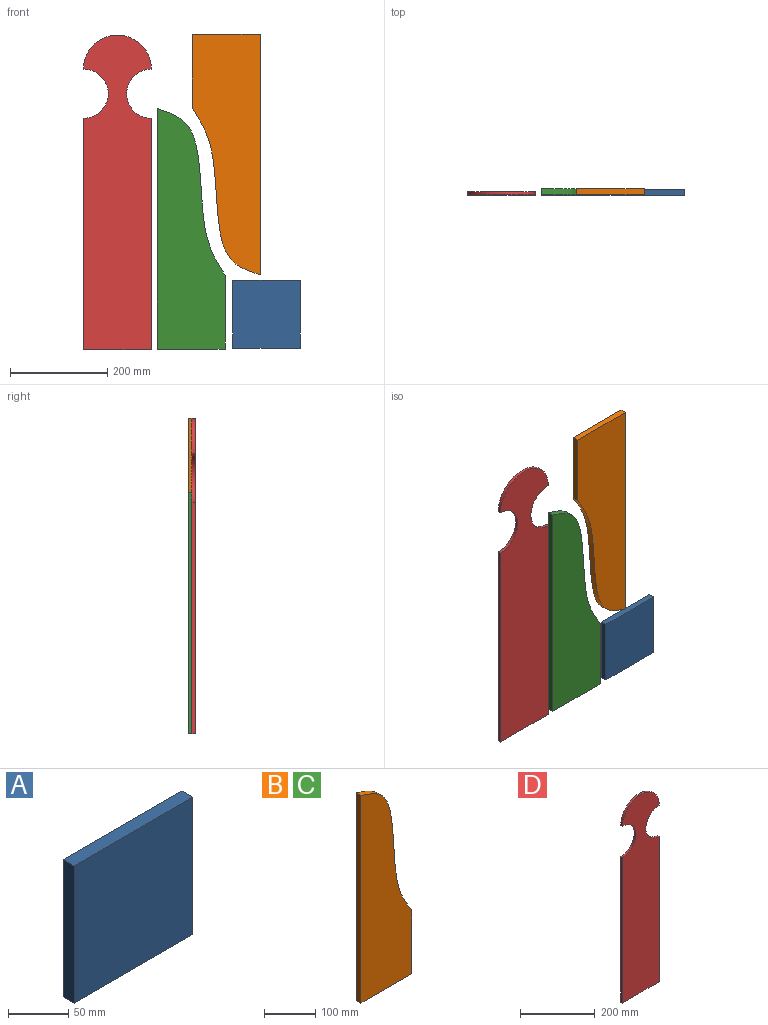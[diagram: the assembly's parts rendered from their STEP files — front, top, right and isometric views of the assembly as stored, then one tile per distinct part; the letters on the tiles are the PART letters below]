
ASSEMBLY  parts=4 mates=3
PART A: 6 faces, bbox 139.7x12.7x139.7 mm
  f0: plane 139.7x12.7mm, normal (-1,0,0), area 1774.2mm2, adj f1,f3,f4,f5
  f1: plane 139.7x12.7mm, normal (0,0,-1), area 1774.2mm2, adj f0,f2,f4,f5
  f2: plane 139.7x12.7mm, normal (1,0,0), area 1774.2mm2, adj f1,f3,f4,f5
  f3: plane 139.7x12.7mm, normal (0,0,1), area 1774.2mm2, adj f0,f2,f4,f5
  f4: plane 139.7x139.7mm, normal (0,-1,0), area 19516.1mm2, adj f0,f1,f2,f3
  f5: plane 139.7x139.7mm, normal (0,1,0), area 19516.1mm2, adj f0,f1,f2,f3
PART B: 6 faces, bbox 139.7x12.7x495.3 mm
  f0: extruded ~342.9x139.7mm, area 5021mm2, adj f1,f3,f4,f5
  f1: plane 495.3x12.7mm, normal (-1,0,0), area 6290.3mm2, adj f0,f2,f4,f5
  f2: plane 139.7x12.7mm, normal (0,0,-1), area 1774.2mm2, adj f1,f3,f4,f5
  f3: plane 152.4x12.7mm, normal (1,0,0), area 1935.5mm2, adj f0,f2,f4,f5
  f4: plane 495.3x139.7mm, normal (0,-1,0), area 52077.9mm2, adj f0,f1,f2,f3
  f5: plane 495.3x139.7mm, normal (0,1,0), area 52077.9mm2, adj f0,f1,f2,f3
PART C: same geometry as B
PART D: 8 faces, bbox 139.7x6.4x647.7 mm
  f0: cylinder r=69.85mm len=139.7mm, axis (0,1,0), area 1393.4mm2, adj f1,f5,f6,f7
  f1: cylinder r=50.8mm len=101.6mm, axis (0,1,0), area 1013.4mm2, adj f0,f2,f6,f7
  f2: plane 476.25x6.35mm, normal (-1,0,0), area 3024.2mm2, adj f1,f3,f6,f7
  f3: plane 139.7x6.35mm, normal (0,0,-1), area 887.1mm2, adj f2,f4,f6,f7
  f4: plane 476.25x6.35mm, normal (1,0,0), area 3024.2mm2, adj f3,f5,f6,f7
  f5: cylinder r=50.8mm len=101.6mm, axis (0,1,0), area 1013.4mm2, adj f0,f4,f6,f7
  f6: plane 647.7x139.7mm, normal (0,-1,0), area 80282.3mm2, adj f0,f1,f2,f3,f4,f5
  f7: plane 647.7x139.7mm, normal (0,1,0), area 80282.3mm2, adj f0,f1,f2,f3,f4,f5
PLACE A t=(-142.31,96.27,-251.33)mm
PLACE B rot(axis=(0,1,0),180deg) t=(-155.38,96.27,147.34)mm
PLACE C t=(-227.79,96.27,-5.55)mm
PLACE D t=(-379.67,89.92,69.62)mm
MATE planar B.f4 <-> C.f4  axis (0,-1,0) through (-142.47,83.57,186.34)mm
MATE planar C.f4 <-> A.f4  axis (0,-1,0) through (-240.7,83.57,-44.55)mm
MATE planar D.f6 <-> B.f4  axis (0,-1,0) through (-309.82,83.57,-16.11)mm
